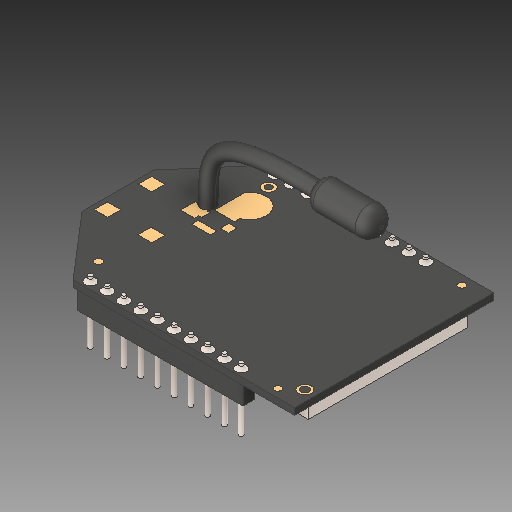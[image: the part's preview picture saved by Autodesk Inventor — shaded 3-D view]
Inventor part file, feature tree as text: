
AUTODESK INVENTOR PART (.ipt)
format: ipt  version: 2017 (Build 210142000, 142)  size: 313,856 bytes
history: mixed  units: mm
features: other x1, fillet x1, imported_body x1
ambient origin geometry x8: Origin, YZ Plane, XZ Plane, XY Plane, X Axis, Y Axis, Z Axis, Center Point
bodies: Body1 (imported_parasolid)
feature tree (3):
  other  "ソリッド1"
  fillet  "Fillet3"  [1 undecoded]
  imported_body  NMx_Import_Brep_tag  [imported B-rep: ~146 faces, bbox_mm=[32.94, 7.5, 23.73]]
note: 1 required parameter value undecoded (feature->parameter linkage not recoverable at this tier; creation-order binding heuristic only, values carry confidence <= 0.55)
